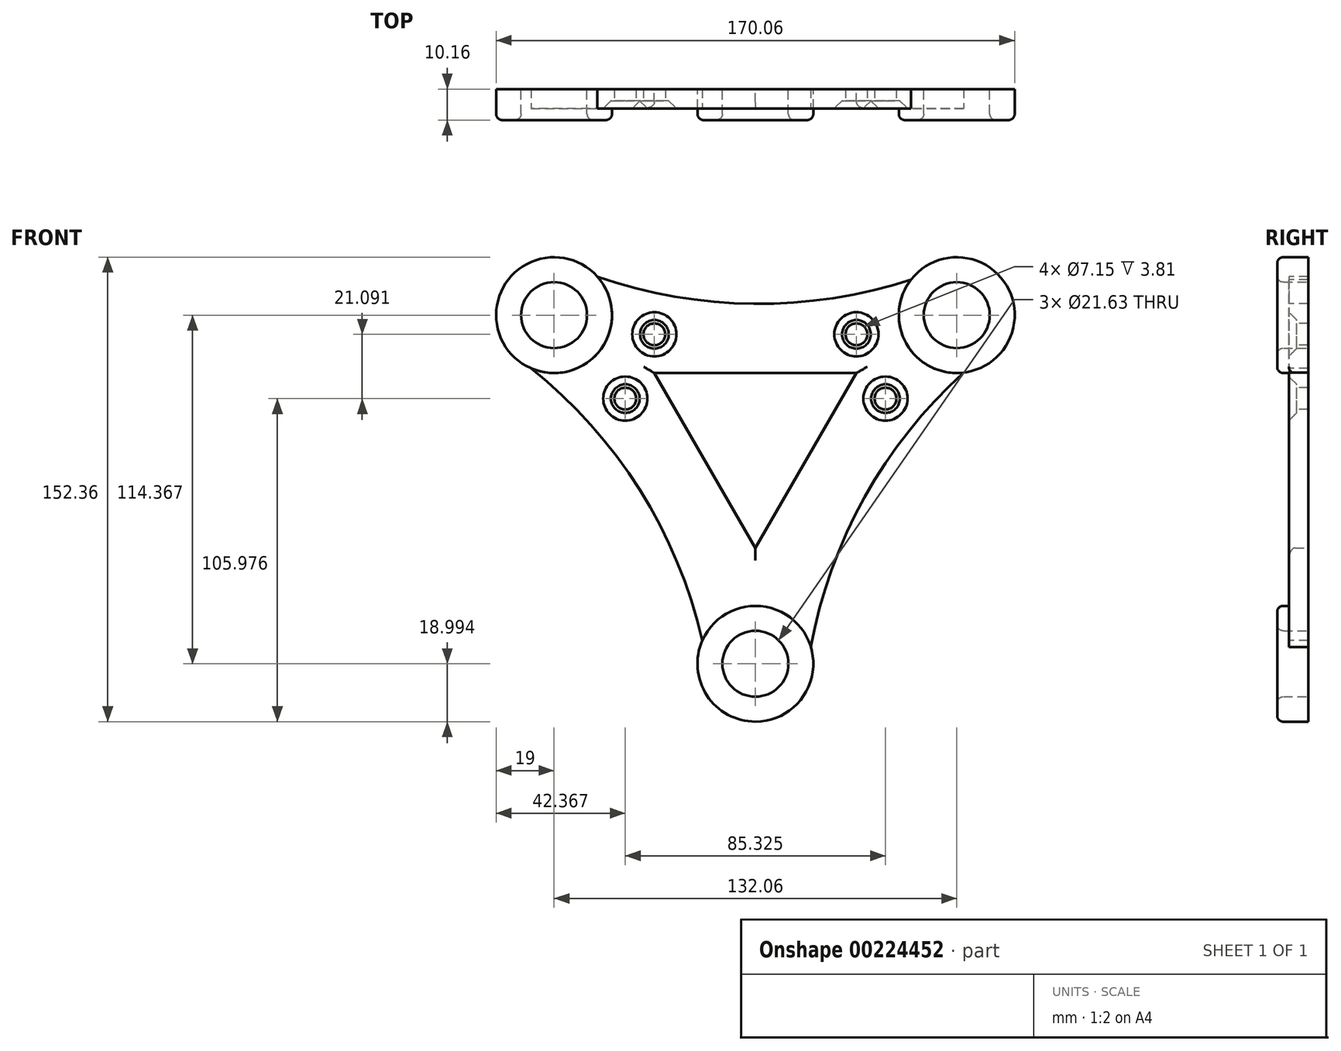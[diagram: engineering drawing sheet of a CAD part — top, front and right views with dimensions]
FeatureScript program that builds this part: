
annotation { "Feature Type Name" : "Feature", "Feature Type Description" : "" }
export const myFeature = defineFeature(function(context is Context, id is Id, definition is map)
    precondition{}
    {
        {
            var Q0;
            Q0=qCreatedBy(makeId("Front.planeOp"),FACE);
            var sketch = newSketch(context, id + "F0", { "sketchPlane" : qUnion([Q0])});
            skCircle(sketch, "E0", {"center": v(-66.03, 46.11) * mm, "radius": 19 * mm});
            skCircle(sketch, "E1", {"center": v(66.03, 46.11) * mm, "radius": 19 * mm});
            skCircle(sketch, "E2", {"center": v(0, -68.26) * mm, "radius": 19 * mm});
            skLineSegment(sketch, "E3", {"start": v(-66.03, 46.11) * mm, "end": v(66.03, 46.11) * mm, "construction": true});
            skLineSegment(sketch, "E4", {"start": v(-66.03, 46.11) * mm, "end": v(0, -68.26) * mm, "construction": true});
            skLineSegment(sketch, "E5", {"start": v(66.03, 46.11) * mm, "end": v(0, -68.26) * mm, "construction": true});
            skLineSegment(sketch, "E6", {"start": v(-66.04, 65.1) * mm, "end": v(66.03, 65.1) * mm});
            skLineSegment(sketch, "E7", {"start": v(-66.03, 27.12) * mm, "end": v(66.03, 27.12) * mm});
            skLineSegment(sketch, "E8", {"start": v(-81.29, 34.8) * mm, "end": v(-14.5, -80.53) * mm});
            skLineSegment(sketch, "E9", {"start": v(-49.58, 55.6) * mm, "end": v(16.45, -58.76) * mm});
            skLineSegment(sketch, "E10", {"start": v(-16.45, -58.76) * mm, "end": v(49.58, 55.6) * mm});
            skLineSegment(sketch, "E11", {"start": v(16.45, -77.75) * mm, "end": v(82.48, 36.61) * mm});
            skSolve(sketch);
        }
        {
            var Q0;
            {var subQ0=sQuery(id+"F0.wireOp",EDGE,"E8");var subQ1=sQuery(id+"F0.wireOp",EDGE,"E2");var subQ2=makeQuery(id+"F0.imprint","INTERSECT",VERTEX,{"disambiguationData":[OD(0.0)],"derivedFrom":[subQ1,subQ0]});Q0=makeQuery(id+"F0.imprint","IMPRINT",FACE,{"disambiguationData":[TD([[makeQuery(id+"F0.imprint","IMPRINT",EDGE,{"disambiguationData":[TD([[subQ2,1.0]])],"derivedFrom":subQ1}),1.0]])]});}
            var Q1;
            {var subQ0=sQuery(id+"F0.wireOp",EDGE,"E0");var subQ1=makeQuery(id+"F0.imprint","INTERSECT",VERTEX,{"derivedFrom":[subQ0,sQuery(id+"F0.wireOp",EDGE,"E6")]});Q1=makeQuery(id+"F0.imprint","IMPRINT",FACE,{"disambiguationData":[TD([[makeQuery(id+"F0.imprint","IMPRINT",EDGE,{"disambiguationData":[TD([[subQ1,1.0]])],"derivedFrom":subQ0}),1.0]])]});}
            var Q2;
            {var subQ0=sQuery(id+"F0.wireOp",EDGE,"E1");var subQ1=makeQuery(id+"F0.imprint","INTERSECT",VERTEX,{"derivedFrom":[subQ0,sQuery(id+"F0.wireOp",EDGE,"E6")]});Q2=makeQuery(id+"F0.imprint","IMPRINT",FACE,{"disambiguationData":[TD([[makeQuery(id+"F0.imprint","IMPRINT",EDGE,{"disambiguationData":[TD([[subQ1,-1.0]])],"derivedFrom":subQ0}),1.0]])]});}
            var Q3;
            {var subQ0=sQuery(id+"F0.wireOp",EDGE,"E2");var subQ1=makeQuery(id+"F0.imprint","INTERSECT",VERTEX,{"derivedFrom":[subQ0,sQuery(id+"F0.wireOp",EDGE,"E9")]});Q3=makeQuery(id+"F0.imprint","IMPRINT",FACE,{"disambiguationData":[TD([[makeQuery(id+"F0.imprint","IMPRINT",EDGE,{"disambiguationData":[TD([[subQ1,-1.0]])],"derivedFrom":subQ0}),1.0]])]});}
            var Q4;
            {var subQ0=sQuery(id+"F0.wireOp",EDGE,"E7");var subQ1=sQuery(id+"F0.wireOp",EDGE,"E0");var subQ2=makeQuery(id+"F0.imprint","INTERSECT",VERTEX,{"derivedFrom":[subQ1,subQ0]});Q4=makeQuery(id+"F0.imprint","IMPRINT",FACE,{"disambiguationData":[TD([[makeQuery(id+"F0.imprint","IMPRINT",EDGE,{"disambiguationData":[TD([[subQ2,1.0]])],"derivedFrom":subQ1}),-1.0]])]});}
            var Q5;
            {var subQ8=sQuery(id+"F0.wireOp",EDGE,"E11");Q5=makeQuery(id+"F0.imprint","IMPRINT",FACE,{"disambiguationData":[TD([[makeQuery(id+"F0.imprint","IMPRINT",EDGE,{"derivedFrom":subQ8}),1.0]])]});}
            var Q6;
            {var subQ5=sQuery(id+"F0.wireOp",EDGE,"E6");Q6=makeQuery(id+"F0.imprint","IMPRINT",FACE,{"disambiguationData":[TD([[makeQuery(id+"F0.imprint","IMPRINT",EDGE,{"derivedFrom":subQ5}),-1.0]])]});}
            var Q7;
            {var subQ0=sQuery(id+"F0.wireOp",EDGE,"E7");var subQ1=sQuery(id+"F0.wireOp",EDGE,"E0");var subQ2=makeQuery(id+"F0.imprint","INTERSECT",VERTEX,{"derivedFrom":[subQ1,subQ0]});Q7=makeQuery(id+"F0.imprint","IMPRINT",FACE,{"disambiguationData":[TD([[makeQuery(id+"F0.imprint","IMPRINT",EDGE,{"disambiguationData":[TD([[subQ2,-1.0]])],"derivedFrom":subQ1}),-1.0]])]});}
            var Q8;
            {var subQ0=sQuery(id+"F0.wireOp",EDGE,"E7");var subQ1=sQuery(id+"F0.wireOp",EDGE,"E1");var subQ2=makeQuery(id+"F0.imprint","INTERSECT",VERTEX,{"derivedFrom":[subQ1,subQ0]});Q8=makeQuery(id+"F0.imprint","IMPRINT",FACE,{"disambiguationData":[TD([[makeQuery(id+"F0.imprint","IMPRINT",EDGE,{"disambiguationData":[TD([[subQ2,1.0]])],"derivedFrom":subQ1}),-1.0]])]});}
            var Q9;
            {var subQ0=sQuery(id+"F0.wireOp",EDGE,"E9");var subQ1=sQuery(id+"F0.wireOp",EDGE,"E2");var subQ2=makeQuery(id+"F0.imprint","INTERSECT",VERTEX,{"derivedFrom":[subQ1,subQ0]});Q9=makeQuery(id+"F0.imprint","IMPRINT",FACE,{"disambiguationData":[TD([[makeQuery(id+"F0.imprint","IMPRINT",EDGE,{"disambiguationData":[TD([[subQ2,-1.0]])],"derivedFrom":subQ1}),-1.0]])]});}
            extrude(context, id + "F1", {"entities" : qUnion([Q0, Q1, Q2, Q3, Q4, Q5, Q6, Q7, Q8, Q9]), "depth" : 6.35 * mm});
        }
        {
            var Q0;
            Q0=makeQuery(id+"F1.opExtrude","CAP_FACE",FACE,{"disambiguationData":[OSD([sQuery(id+"F0.wireOp",EDGE,"E0"),sQuery(id+"F0.wireOp",EDGE,"E1"),sQuery(id+"F0.wireOp",EDGE,"E2"),sQuery(id+"F0.wireOp",EDGE,"E6"),sQuery(id+"F0.wireOp",EDGE,"E7"),sQuery(id+"F0.wireOp",EDGE,"E8"),sQuery(id+"F0.wireOp",EDGE,"E9"),sQuery(id+"F0.wireOp",EDGE,"E10"),sQuery(id+"F0.wireOp",EDGE,"E11")])],"isStart":false});
            var sketch = newSketch(context, id + "F2", { "sketchPlane" : qUnion([Q0])});
            skCircle(sketch, "E12.0", {"center": v(66.03, 46.11) * mm, "radius": 19 * mm});
            skCircle(sketch, "E12.1", {"center": v(-66.03, 46.11) * mm, "radius": 19 * mm});
            skCircle(sketch, "E12.2", {"center": v(0, -68.26) * mm, "radius": 19 * mm});
            skCircle(sketch, "E13", {"center": v(-66.03, 46.11) * mm, "radius": 10.81 * mm});
            skCircle(sketch, "E14", {"center": v(66.03, 46.11) * mm, "radius": 10.81 * mm});
            skCircle(sketch, "E15", {"center": v(0, -68.26) * mm, "radius": 10.81 * mm});
            skSolve(sketch);
        }
        {
            var Q0;
            Q0 = qSketchRegion(id + "F2", true);
            extrude(context, id + "F3", {"entities" : qUnion([Q0]), "operationType" : NewBodyOperationType.ADD, "depth" : 3.8 * mm});
        }
        {
            var Q0;
            Q0=makeQuery(id+"F2.imprint","IMPRINT",FACE,{"disambiguationData":[TD([[makeQuery(id+"F2.imprint","IMPRINT",EDGE,{"derivedFrom":sQuery(id+"F2.wireOp",EDGE,"E13")}),1.0]])]});
            var Q1;
            Q1=makeQuery(id+"F2.imprint","IMPRINT",FACE,{"disambiguationData":[TD([[makeQuery(id+"F2.imprint","IMPRINT",EDGE,{"derivedFrom":sQuery(id+"F2.wireOp",EDGE,"E14")}),1.0]])]});
            var Q2;
            Q2=makeQuery(id+"F2.imprint","IMPRINT",FACE,{"disambiguationData":[TD([[makeQuery(id+"F2.imprint","IMPRINT",EDGE,{"derivedFrom":sQuery(id+"F2.wireOp",EDGE,"E15")}),1.0]])]});
            extrude(context, id + "F4", {"entities" : qUnion([Q0, Q1, Q2]), "operationType" : NewBodyOperationType.REMOVE, "endBound" : BoundingType.THROUGH_ALL, "oppositeDirection" : true, "depth" : 25.4 * mm});
        }
        {
            var Q0;
            Q0=makeQuery(id+"F3.opExtrude","CAP_EDGE",EDGE,{"disambiguationData":[OSD([sQuery(id+"F2.wireOp",EDGE,"E12.1")])],"isStart":false});
            fillet(context, id + "F5", {"entities" : qUnion([Q0]), "radius" : 2.03 * mm, "tangentPropagation" : true, "allowEdgeOverflow" : false});
        }
        {
            var Q0;
            Q0=makeQuery(id+"F3.opExtrude","CAP_EDGE",EDGE,{"disambiguationData":[OSD([sQuery(id+"F2.wireOp",EDGE,"E13")])],"isStart":false});
            fillet(context, id + "F6", {"entities" : qUnion([Q0]), "radius" : 2.03 * mm, "tangentPropagation" : true, "allowEdgeOverflow" : false});
        }
        {
            var Q0;
            Q0=makeQuery(id+"F3.opExtrude","CAP_EDGE",EDGE,{"disambiguationData":[OSD([sQuery(id+"F2.wireOp",EDGE,"E12.0")])],"isStart":false});
            var Q1;
            Q1=makeQuery(id+"F3.opExtrude","CAP_EDGE",EDGE,{"disambiguationData":[OSD([sQuery(id+"F2.wireOp",EDGE,"E12.2")])],"isStart":false});
            var Q2;
            Q2=makeQuery(id+"F3.opExtrude","CAP_EDGE",EDGE,{"disambiguationData":[OSD([sQuery(id+"F2.wireOp",EDGE,"E14")])],"isStart":false});
            var Q3;
            Q3=makeQuery(id+"F3.opExtrude","CAP_EDGE",EDGE,{"disambiguationData":[OSD([sQuery(id+"F2.wireOp",EDGE,"E15")])],"isStart":false});
            fillet(context, id + "F7", {"entities" : qUnion([Q0, Q1, Q2, Q3]), "radius" : 2.03 * mm, "tangentPropagation" : true, "allowEdgeOverflow" : false});
        }
        {
            var Q0;
            {var subQ0=sQuery(id+"F0.wireOp",EDGE,"E10");var subQ1=sQuery(id+"F0.wireOp",EDGE,"E9");var subQ2=sQuery(id+"F0.wireOp",EDGE,"E8");var subQ3=sQuery(id+"F0.wireOp",EDGE,"E7");var subQ4=sQuery(id+"F0.wireOp",EDGE,"E0");var subQ5=sQuery(id+"F0.wireOp",EDGE,"E11");var subQ6=sQuery(id+"F0.wireOp",EDGE,"E1");var subQ7=sQuery(id+"F0.wireOp",EDGE,"E2");var subQ8=sQuery(id+"F0.wireOp",EDGE,"E6");Q0=makeQuery(id+"F3.boolean.opBoolean","SPLIT",FACE,{"disambiguationData":[TD([makeQuery(id+"F1.opExtrude","SWEPT_FACE",FACE,{"disambiguationData":[OSD([subQ4])]})])],"derivedFrom":makeQuery(id+"F1.opExtrude","CAP_FACE",FACE,{"disambiguationData":[OSD([subQ4,subQ6,subQ7,subQ8,subQ3,subQ2,subQ1,subQ0,subQ5])],"isStart":false})});}
            var sketch = newSketch(context, id + "F8", { "sketchPlane" : qUnion([Q0])});
            skArc(sketch, "E16", {"start": v(-51.9, 58.82) * mm, "mid": v(-0.5, 49.82) * mm, "end": v(51.06, 57.8) * mm});
            skArc(sketch, "E17", {"start": v(-17.38, -60.6) * mm, "mid": v(-37.93, -11.2) * mm, "end": v(-73.59, 28.69) * mm});
            skArc(sketch, "E18", {"start": v(68.3, 27.25) * mm, "mid": v(35.81, -13.6) * mm, "end": v(18.17, -62.73) * mm});
            skSolve(sketch);
        }
        {
            var Q0;
            {var subQ0=sQuery(id+"F8.wireOp",EDGE,"E18");Q0=makeQuery(id+"F8.imprint","IMPRINT",FACE,{"disambiguationData":[TD([[makeQuery(id+"F8.imprint","IMPRINT",EDGE,{"derivedFrom":subQ0}),1.0]])]});}
            var Q1;
            {var subQ0=sQuery(id+"F8.wireOp",EDGE,"E16");Q1=makeQuery(id+"F8.imprint","IMPRINT",FACE,{"disambiguationData":[TD([[makeQuery(id+"F8.imprint","IMPRINT",EDGE,{"derivedFrom":subQ0}),1.0]])]});}
            var Q2;
            {var subQ0=sQuery(id+"F8.wireOp",EDGE,"E17");Q2=makeQuery(id+"F8.imprint","IMPRINT",FACE,{"disambiguationData":[TD([[makeQuery(id+"F8.imprint","IMPRINT",EDGE,{"derivedFrom":subQ0}),1.0]])]});}
            extrude(context, id + "F9", {"entities" : qUnion([Q0, Q1, Q2]), "operationType" : NewBodyOperationType.REMOVE, "endBound" : BoundingType.THROUGH_ALL, "oppositeDirection" : true, "depth" : 25.4 * mm});
        }
        {
            var Q0;
            {var subQ0=sQuery(id+"F0.wireOp",EDGE,"E10");var subQ1=sQuery(id+"F0.wireOp",EDGE,"E9");var subQ2=sQuery(id+"F0.wireOp",EDGE,"E8");var subQ3=sQuery(id+"F0.wireOp",EDGE,"E7");var subQ4=sQuery(id+"F0.wireOp",EDGE,"E0");var subQ5=sQuery(id+"F0.wireOp",EDGE,"E11");var subQ6=sQuery(id+"F0.wireOp",EDGE,"E1");var subQ7=sQuery(id+"F0.wireOp",EDGE,"E2");var subQ8=sQuery(id+"F0.wireOp",EDGE,"E6");Q0=makeQuery(id+"F3.boolean.opBoolean","SPLIT",FACE,{"disambiguationData":[TD([makeQuery(id+"F1.opExtrude","SWEPT_FACE",FACE,{"disambiguationData":[OSD([subQ4])]})])],"derivedFrom":makeQuery(id+"F1.opExtrude","CAP_FACE",FACE,{"disambiguationData":[OSD([subQ4,subQ6,subQ7,subQ8,subQ3,subQ2,subQ1,subQ0,subQ5])],"isStart":false})});}
            var sketch = newSketch(context, id + "F10", { "sketchPlane" : qUnion([Q0])});
            skLineSegment(sketch, "E19", {"start": v(0, -30.27) * mm, "end": v(0, -49.26) * mm, "construction": true});
            skCircle(sketch, "E20", {"center": v(-33.13, 39.82) * mm, "radius": 5.97 * mm});
            skCircle(sketch, "E21", {"center": v(-42.66, 18.73) * mm, "radius": 5.97 * mm});
            skCircle(sketch, "E22", {"center": v(33.13, 39.82) * mm, "radius": 5.97 * mm});
            skCircle(sketch, "E23", {"center": v(42.66, 18.73) * mm, "radius": 5.97 * mm});
            skCircle(sketch, "E24", {"center": v(-33.13, 39.82) * mm, "radius": 3.57 * mm});
            skCircle(sketch, "E25", {"center": v(-42.66, 18.73) * mm, "radius": 3.57 * mm});
            skCircle(sketch, "E26", {"center": v(33.13, 39.82) * mm, "radius": 3.57 * mm});
            skCircle(sketch, "E27", {"center": v(42.66, 18.73) * mm, "radius": 3.57 * mm});
            skSolve(sketch);
        }
        {
            var Q0;
            Q0=makeQuery(id+"F9.boolean.opBoolean","COPY",EDGE,{"derivedFrom":makeQuery(id+"F9.opExtrude","CAP_EDGE",EDGE,{"disambiguationData":[OSD([sQuery(id+"F8.wireOp",EDGE,"E16")])],"isStart":true})});
            var Q1;
            Q1=makeQuery(id+"F9.boolean.opBoolean","COPY",EDGE,{"derivedFrom":makeQuery(id+"F9.opExtrude","CAP_EDGE",EDGE,{"disambiguationData":[OSD([sQuery(id+"F8.wireOp",EDGE,"E17")])],"isStart":true})});
            var Q2;
            Q2=makeQuery(id+"F9.boolean.opBoolean","COPY",EDGE,{"derivedFrom":makeQuery(id+"F9.opExtrude","CAP_EDGE",EDGE,{"disambiguationData":[OSD([sQuery(id+"F8.wireOp",EDGE,"E18")])],"isStart":true})});
            var Q3;
            Q3=makeQuery(id+"F1.opExtrude","CAP_EDGE",EDGE,{"disambiguationData":[OSD([sQuery(id+"F0.wireOp",EDGE,"E7")])],"isStart":false});
            var Q4;
            Q4=makeQuery(id+"F1.opExtrude","CAP_EDGE",EDGE,{"disambiguationData":[OSD([sQuery(id+"F0.wireOp",EDGE,"E9")])],"isStart":false});
            var Q5;
            Q5=makeQuery(id+"F1.opExtrude","CAP_EDGE",EDGE,{"disambiguationData":[OSD([sQuery(id+"F0.wireOp",EDGE,"E10")])],"isStart":false});
            fillet(context, id + "F11", {"entities" : qUnion([Q0, Q1, Q2, Q3, Q4, Q5]), "radius" : 2.03 * mm, "tangentPropagation" : true, "allowEdgeOverflow" : false});
        }
        {
            var Q0;
            Q0=makeQuery(id+"F10.imprint","IMPRINT",FACE,{"disambiguationData":[TD([[makeQuery(id+"F10.imprint","IMPRINT",EDGE,{"derivedFrom":makeQuery(id+"F1.opExtrude","CAP_EDGE",EDGE,{"disambiguationData":[OSD([sQuery(id+"F0.wireOp",EDGE,"E7")])],"isStart":false})}),1.0]])]});
            var sketch = newSketch(context, id + "F12", { "sketchPlane" : qUnion([Q0])});
            skSolve(sketch);
        }
        {
            var Q0;
            Q0=makeQuery(id+"F10.imprint","IMPRINT",FACE,{"disambiguationData":[TD([[makeQuery(id+"F10.imprint","IMPRINT",EDGE,{"derivedFrom":sQuery(id+"F10.wireOp",EDGE,"E24")}),1.0]])]});
            var Q1;
            Q1=makeQuery(id+"F10.imprint","IMPRINT",FACE,{"disambiguationData":[TD([[makeQuery(id+"F10.imprint","IMPRINT",EDGE,{"derivedFrom":sQuery(id+"F10.wireOp",EDGE,"E25")}),1.0]])]});
            var Q2;
            Q2=makeQuery(id+"F10.imprint","IMPRINT",FACE,{"disambiguationData":[TD([[makeQuery(id+"F10.imprint","IMPRINT",EDGE,{"derivedFrom":sQuery(id+"F10.wireOp",EDGE,"E26")}),1.0]])]});
            var Q3;
            Q3=makeQuery(id+"F10.imprint","IMPRINT",FACE,{"disambiguationData":[TD([[makeQuery(id+"F10.imprint","IMPRINT",EDGE,{"derivedFrom":sQuery(id+"F10.wireOp",EDGE,"E27")}),1.0]])]});
            extrude(context, id + "F13", {"entities" : qUnion([Q0, Q1, Q2, Q3]), "operationType" : NewBodyOperationType.REMOVE, "endBound" : BoundingType.THROUGH_ALL, "oppositeDirection" : true, "depth" : 25.4 * mm});
        }
        {
            var Q0;
            Q0=makeQuery(id+"F10.imprint","IMPRINT",FACE,{"disambiguationData":[TD([[makeQuery(id+"F10.imprint","IMPRINT",EDGE,{"derivedFrom":sQuery(id+"F10.wireOp",EDGE,"E20")}),1.0]])]});
            var Q1;
            Q1=makeQuery(id+"F10.imprint","IMPRINT",FACE,{"disambiguationData":[TD([[makeQuery(id+"F10.imprint","IMPRINT",EDGE,{"derivedFrom":sQuery(id+"F10.wireOp",EDGE,"E21")}),1.0]])]});
            var Q2;
            Q2=makeQuery(id+"F10.imprint","IMPRINT",FACE,{"disambiguationData":[TD([[makeQuery(id+"F10.imprint","IMPRINT",EDGE,{"derivedFrom":sQuery(id+"F10.wireOp",EDGE,"E22")}),1.0]])]});
            var Q3;
            Q3=makeQuery(id+"F10.imprint","IMPRINT",FACE,{"disambiguationData":[TD([[makeQuery(id+"F10.imprint","IMPRINT",EDGE,{"derivedFrom":sQuery(id+"F10.wireOp",EDGE,"E23")}),1.0]])]});
            extrude(context, id + "F14", {"entities" : qUnion([Q0, Q1, Q2, Q3]), "operationType" : NewBodyOperationType.REMOVE, "oppositeDirection" : true, "depth" : 2.54 * mm});
        }
        {
            var Q0;
            Q0=makeQuery(id+"F14.boolean.opBoolean","COPY",FACE,{"derivedFrom":makeQuery(id+"F14.opExtrude","SWEPT_FACE",FACE,{"disambiguationData":[OSD([sQuery(id+"F10.wireOp",EDGE,"E20")])]})});
            var Q1;
            Q1=makeQuery(id+"F14.boolean.opBoolean","COPY",FACE,{"derivedFrom":makeQuery(id+"F14.opExtrude","SWEPT_FACE",FACE,{"disambiguationData":[OSD([sQuery(id+"F10.wireOp",EDGE,"E21")])]})});
            var Q2;
            Q2=makeQuery(id+"F14.boolean.opBoolean","COPY",FACE,{"derivedFrom":makeQuery(id+"F14.opExtrude","SWEPT_FACE",FACE,{"disambiguationData":[OSD([sQuery(id+"F10.wireOp",EDGE,"E22")])]})});
            var Q3;
            Q3=makeQuery(id+"F14.boolean.opBoolean","COPY",FACE,{"derivedFrom":makeQuery(id+"F14.opExtrude","SWEPT_FACE",FACE,{"disambiguationData":[OSD([sQuery(id+"F10.wireOp",EDGE,"E23")])]})});
            chamfer(context, id + "F15", {"entities" : qUnion([Q0, Q1, Q2, Q3]), "width" : 1.27 * mm, "tangentPropagation" : true});
        }
    });
